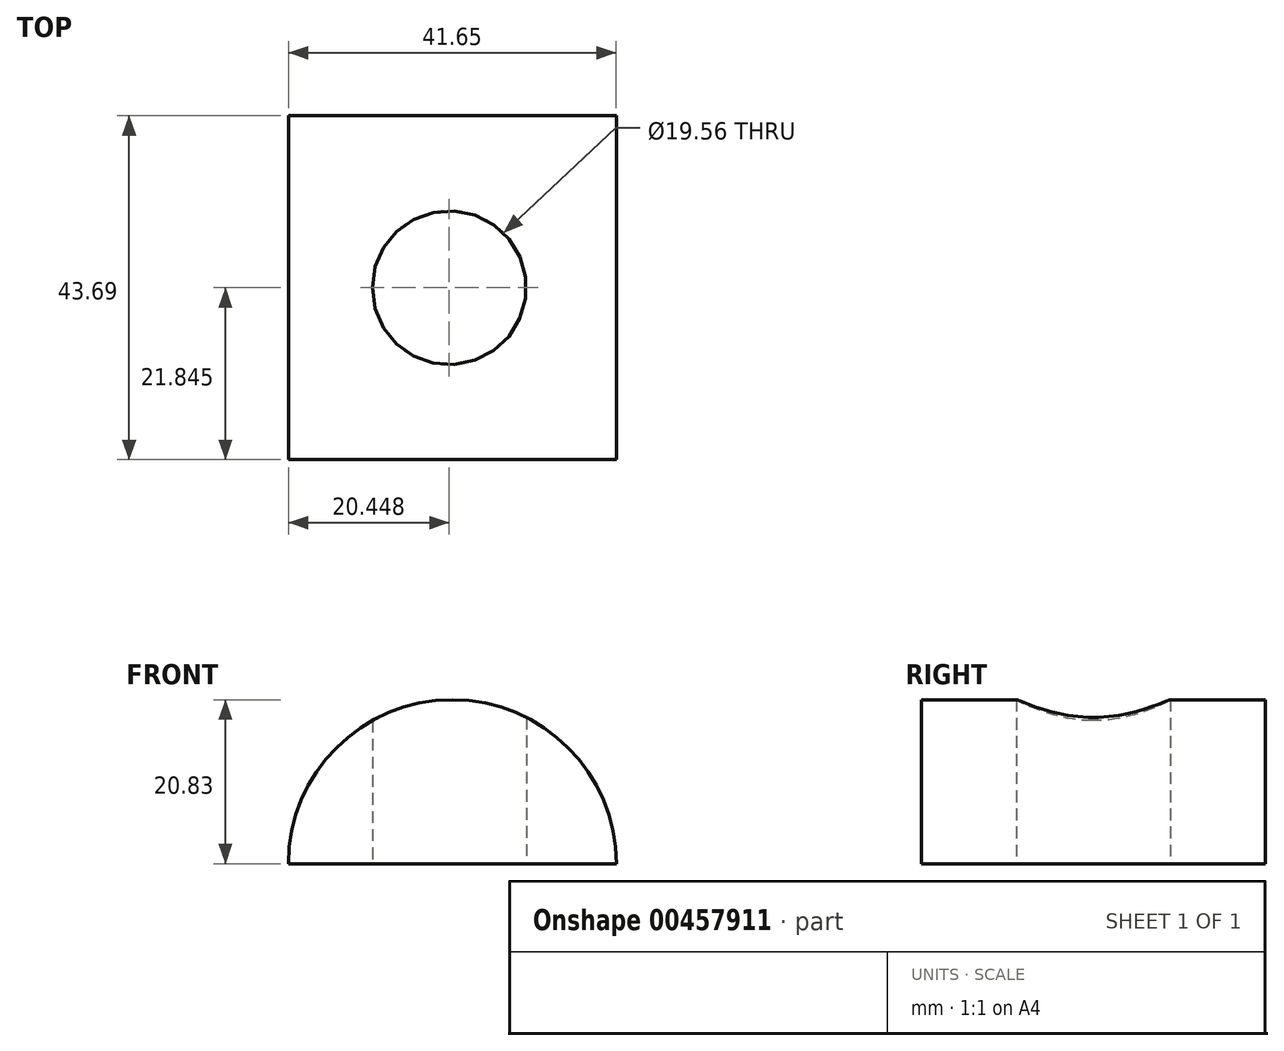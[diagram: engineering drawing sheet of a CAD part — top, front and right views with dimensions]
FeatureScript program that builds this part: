
annotation { "Feature Type Name" : "Feature", "Feature Type Description" : "" }
export const myFeature = defineFeature(function(context is Context, id is Id, definition is map)
    precondition{}
    {
        {
            var Q0;
            Q0=qCreatedBy(makeId("Top.planeOp"),FACE);
            var sketch = newSketch(context, id + "F0", { "sketchPlane" : qUnion([Q0])});
            skLineSegment(sketch, "E0.bottom", {"start": v(-19.88, 16.26) * mm, "end": v(23.3, 16.26) * mm});
            skLineSegment(sketch, "E0.top", {"start": v(-19.88, -27.43) * mm, "end": v(23.3, -27.43) * mm});
            skLineSegment(sketch, "E0.left", {"start": v(-19.88, 16.26) * mm, "end": v(-19.88, -27.43) * mm});
            skLineSegment(sketch, "E0.right", {"start": v(23.3, 16.26) * mm, "end": v(23.3, -27.43) * mm});
            skLineSegment(sketch, "E1", {"start": v(-19.88, -5.58) * mm, "end": v(1.33, -5.58) * mm, "construction": true});
            skCircle(sketch, "E2", {"center": v(1.33, -5.58) * mm, "radius": 9.78 * mm});
            skSolve(sketch);
        }
        {
            var Q0;
            Q0 = qSketchRegion(id + "F0", true);
            extrude(context, id + "F1", {"entities" : qUnion([Q0]), "depth" : 20.83 * mm});
        }
        {
            var Q0;
            Q0=makeQuery(id+"F1.opExtrude","SWEPT_FACE",FACE,{"disambiguationData":[OSD([sQuery(id+"F0.wireOp",EDGE,"E0.top")])]});
            var sketch = newSketch(context, id + "F2", { "sketchPlane" : qUnion([Q0])});
            skArc(sketch, "E3", {"start": v(22.53, 0) * mm, "mid": v(1.7, 20.83) * mm, "end": v(-19.12, 0) * mm});
            skSolve(sketch);
        }
        {
            var Q0;
            {var subQ3=sQuery(id+"F2.wireOp",EDGE,"E3");Q0=makeQuery(id+"F2.imprint","IMPRINT",FACE,{"disambiguationData":[TD([[makeQuery(id+"F2.imprint","IMPRINT",EDGE,{"derivedFrom":subQ3}),-1.0]])]});}
            extrude(context, id + "F3", {"entities" : qUnion([Q0]), "operationType" : NewBodyOperationType.REMOVE, "endBound" : BoundingType.THROUGH_ALL, "oppositeDirection" : true, "depth" : 25.4 * mm});
        }
    });
